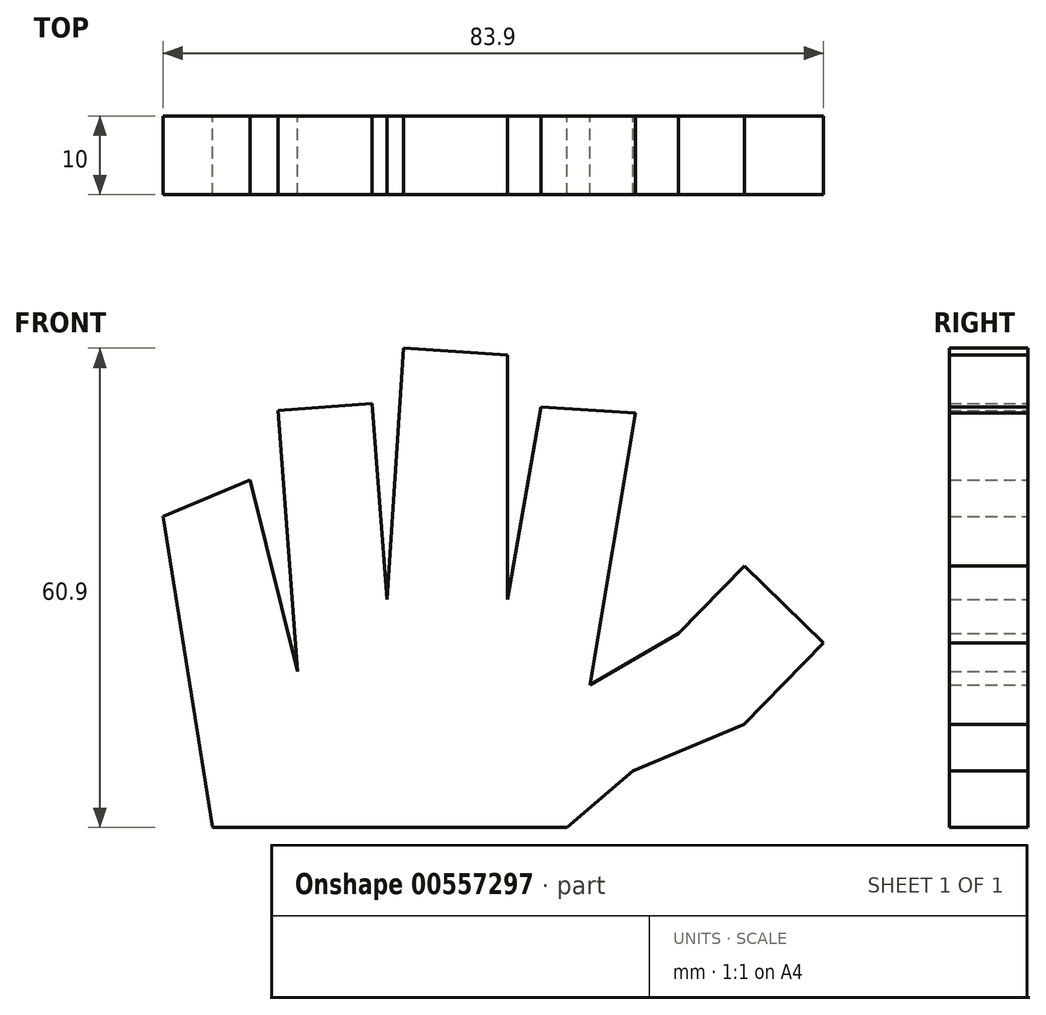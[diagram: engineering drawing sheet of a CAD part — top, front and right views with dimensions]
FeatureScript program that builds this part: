
annotation { "Feature Type Name" : "Feature", "Feature Type Description" : "" }
export const myFeature = defineFeature(function(context is Context, id is Id, definition is map)
    precondition{}
    {
        {
            var Q0;
            Q0=qCreatedBy(makeId("Front.planeOp"),FACE);
            var sketch = newSketch(context, id + "F0", { "sketchPlane" : qUnion([Q0])});
            skLineSegment(sketch, "E0", {"start": v(0, 0) * mm, "end": v(-45, 0) * mm});
            skLineSegment(sketch, "E1", {"start": v(-45, 0) * mm, "end": v(-51.3, 39.5) * mm});
            skLineSegment(sketch, "E2", {"start": v(-51.3, 39.5) * mm, "end": v(-40.24, 44.12) * mm});
            skLineSegment(sketch, "E3", {"start": v(-40.24, 44.12) * mm, "end": v(-34.2, 19.86) * mm});
            skLineSegment(sketch, "E4", {"start": v(-34.2, 19.86) * mm, "end": v(-36.71, 53) * mm});
            skLineSegment(sketch, "E5", {"start": v(-36.71, 53) * mm, "end": v(-24.74, 53.9) * mm});
            skLineSegment(sketch, "E6", {"start": v(-24.74, 53.9) * mm, "end": v(-22.86, 28.97) * mm});
            skLineSegment(sketch, "E7", {"start": v(-22.86, 28.97) * mm, "end": v(-20.77, 60.9) * mm});
            skLineSegment(sketch, "E8", {"start": v(-20.77, 60.9) * mm, "end": v(-7.52, 60.04) * mm});
            skLineSegment(sketch, "E9", {"start": v(-7.52, 60.04) * mm, "end": v(-7.52, 28.97) * mm});
            skLineSegment(sketch, "E10", {"start": v(-7.52, 28.97) * mm, "end": v(-3.26, 53.45) * mm});
            skPoint(sketch, "E10.endSnap0", {"position": v(-30.73, 53.45) * mm});
            skLineSegment(sketch, "E11", {"start": v(-3.26, 53.45) * mm, "end": v(8.72, 52.66) * mm});
            skLineSegment(sketch, "E12", {"start": v(8.72, 52.66) * mm, "end": v(2.93, 18.15) * mm});
            skLineSegment(sketch, "E13", {"start": v(2.93, 18.15) * mm, "end": v(14.19, 24.64) * mm});
            skLineSegment(sketch, "E14", {"start": v(14.19, 24.64) * mm, "end": v(22.57, 33.23) * mm});
            skLineSegment(sketch, "E15", {"start": v(22.57, 33.23) * mm, "end": v(32.59, 23.45) * mm});
            skLineSegment(sketch, "E16", {"start": v(32.59, 23.45) * mm, "end": v(22.48, 13.09) * mm});
            skLineSegment(sketch, "E17", {"start": v(22.48, 13.09) * mm, "end": v(8.4, 7.2) * mm});
            skLineSegment(sketch, "E18", {"start": v(8.4, 7.2) * mm, "end": v(0, 0) * mm});
            skSolve(sketch);
        }
        {
            var Q0;
            Q0=makeQuery(id+"F0.imprint","IMPRINT",FACE,{"disambiguationData":[TD([[makeQuery(id+"F0.imprint","IMPRINT",EDGE,{"derivedFrom":sQuery(id+"F0.wireOp",EDGE,"E0")}),-1.0]])]});
            extrude(context, id + "F1", {"entities" : qUnion([Q0]), "endBound" : BoundingType.SYMMETRIC, "depth" : 10 * mm, "offsetDistance" : 25 * mm});
        }
    });
